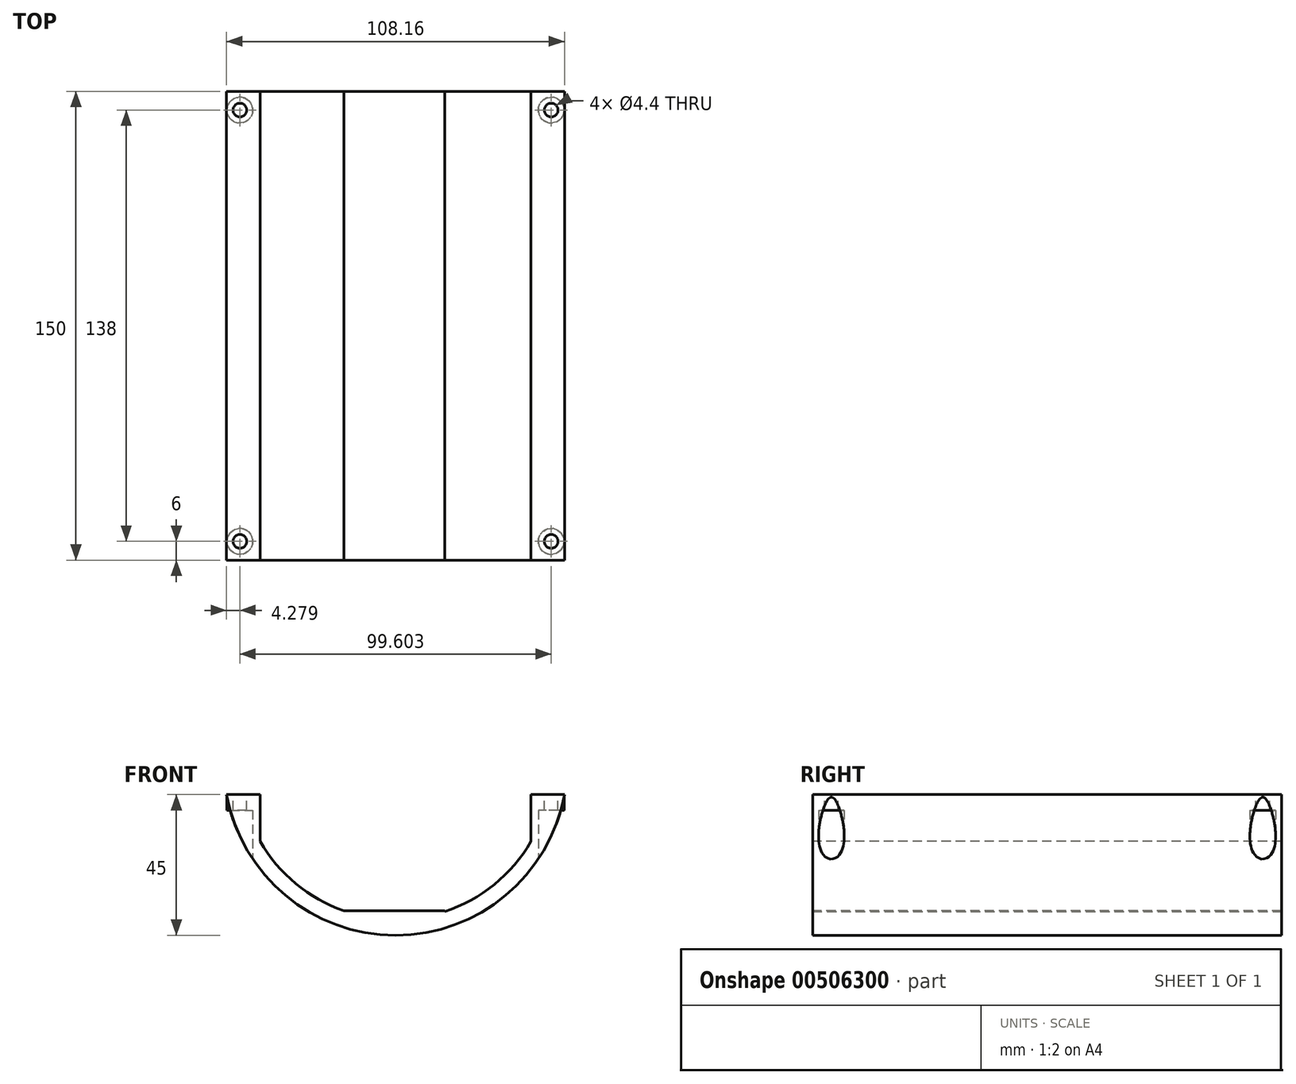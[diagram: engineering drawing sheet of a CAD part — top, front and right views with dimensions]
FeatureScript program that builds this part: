
annotation { "Feature Type Name" : "Feature", "Feature Type Description" : "" }
export const myFeature = defineFeature(function(context is Context, id is Id, definition is map)
    precondition{}
    {
        {
            var Q0;
            Q0=qCreatedBy(makeId("Front.planeOp"),FACE);
            var sketch = newSketch(context, id + "F0", { "sketchPlane" : qUnion([Q0])});
            skCircle(sketch, "E0", {"center": v(0, 0) * mm, "radius": 50 * mm});
            skCircle(sketch, "E1.0", {"center": v(0, 0) * mm, "radius": 55 * mm});
            skSolve(sketch);
        }
        {
            var Q0;
            Q0 = qSketchRegion(id + "F0", true);
            extrude(context, id + "F1", {"entities" : qUnion([Q0]), "depth" : 150 * mm});
        }
        {
            var Q0;
            Q0=makeQuery(id+"F1.opExtrude","CAP_FACE",FACE,{"disambiguationData":[OSD([sQuery(id+"F0.wireOp",EDGE,"E0"),sQuery(id+"F0.wireOp",EDGE,"E1.0")])],"isStart":false});
            var sketch = newSketch(context, id + "F2", { "sketchPlane" : qUnion([Q0])});
            skLineSegment(sketch, "E2.bottom", {"start": v(-54.77, -5) * mm, "end": v(54.77, -5) * mm});
            skLineSegment(sketch, "E2.top", {"start": v(-54.08, -10) * mm, "end": v(54.08, -10) * mm});
            skArc(sketch, "E3.0", {"start": v(-54.77, -5) * mm, "mid": v(-54.49, -7.5) * mm, "end": v(-54.08, -10) * mm});
            skArc(sketch, "E4.trimOffspring", {"start": v(54.08, -10) * mm, "mid": v(54.49, -7.5) * mm, "end": v(54.77, -5) * mm});
            skSolve(sketch);
        }
        {
            var Q0;
            Q0 = qSketchRegion(id + "F2", true);
            extrude(context, id + "F3", {"entities" : qUnion([Q0]), "operationType" : NewBodyOperationType.ADD, "oppositeDirection" : true, "depth" : 150 * mm});
        }
        {
            var Q0;
            Q0=makeQuery(id+"F3.boolean.opBoolean","MERGE",FACE,{"derivedFrom":[makeQuery(id+"F1.opExtrude","CAP_FACE",FACE,{"disambiguationData":[OSD([sQuery(id+"F0.wireOp",EDGE,"E0"),sQuery(id+"F0.wireOp",EDGE,"E1.0")])],"isStart":false}),makeQuery(id+"F3.opExtrude","CAP_FACE",FACE,{"disambiguationData":[OSD([sQuery(id+"F2.wireOp",EDGE,"E2.bottom"),sQuery(id+"F2.wireOp",EDGE,"E2.top"),sQuery(id+"F2.wireOp",EDGE,"E3.0"),sQuery(id+"F2.wireOp",EDGE,"E4.trimOffspring")])],"isStart":true})]});
            var sketch = newSketch(context, id + "F4", { "sketchPlane" : qUnion([Q0])});
            skLineSegment(sketch, "E5", {"start": v(-48.99, 25) * mm, "end": v(48.99, 25) * mm});
            skLineSegment(sketch, "E6", {"start": v(-46.1, 30) * mm, "end": v(46.1, 30) * mm});
            skArc(sketch, "E7.0", {"start": v(48.99, 25) * mm, "mid": v(47.6, 27.54) * mm, "end": v(46.1, 30) * mm});
            skArc(sketch, "E8.trimOffspring", {"start": v(-46.1, 30) * mm, "mid": v(-47.6, 27.54) * mm, "end": v(-48.99, 25) * mm});
            skSolve(sketch);
        }
        {
            var Q0;
            Q0 = qSketchRegion(id + "F4", true);
            extrude(context, id + "F5", {"entities" : qUnion([Q0]), "operationType" : NewBodyOperationType.ADD, "oppositeDirection" : true, "depth" : 150 * mm});
        }
        {
            var Q0;
            Q0=makeQuery(id+"F5.boolean.opBoolean","MERGE",FACE,{"derivedFrom":[makeQuery(id+"F3.boolean.opBoolean","MERGE",FACE,{"derivedFrom":[makeQuery(id+"F1.opExtrude","CAP_FACE",FACE,{"disambiguationData":[OSD([sQuery(id+"F0.wireOp",EDGE,"E0"),sQuery(id+"F0.wireOp",EDGE,"E1.0")])],"isStart":false}),makeQuery(id+"F3.opExtrude","CAP_FACE",FACE,{"disambiguationData":[OSD([sQuery(id+"F2.wireOp",EDGE,"E2.bottom"),sQuery(id+"F2.wireOp",EDGE,"E2.top"),sQuery(id+"F2.wireOp",EDGE,"E3.0"),sQuery(id+"F2.wireOp",EDGE,"E4.trimOffspring")])],"isStart":true})]}),makeQuery(id+"F5.opExtrude","CAP_FACE",FACE,{"disambiguationData":[OSD([sQuery(id+"F4.wireOp",EDGE,"E5"),sQuery(id+"F4.wireOp",EDGE,"E6"),sQuery(id+"F4.wireOp",EDGE,"E7.0"),sQuery(id+"F4.wireOp",EDGE,"E8.trimOffspring")])],"isStart":true})]});
            var sketch = newSketch(context, id + "F6", { "sketchPlane" : qUnion([Q0])});
            skLineSegment(sketch, "E9", {"start": v(-40, 30) * mm, "end": v(108.18, 30) * mm});
            skLineSegment(sketch, "E10", {"start": v(108.18, 30) * mm, "end": v(0, 63.47) * mm});
            skLineSegment(sketch, "E11", {"start": v(0, 63.47) * mm, "end": v(-68.98, 30) * mm});
            skLineSegment(sketch, "E12", {"start": v(-68.98, 30) * mm, "end": v(-40, 30) * mm});
            skSolve(sketch);
        }
        {
            var Q0;
            Q0 = qSketchRegion(id + "F6", true);
            extrude(context, id + "F7", {"entities" : qUnion([Q0]), "operationType" : NewBodyOperationType.REMOVE, "oppositeDirection" : true, "depth" : 233.5 * mm});
        }
        {
            var Q0;
            Q0=makeQuery(id+"F5.boolean.opBoolean","MERGE",FACE,{"derivedFrom":[makeQuery(id+"F3.boolean.opBoolean","MERGE",FACE,{"derivedFrom":[makeQuery(id+"F1.opExtrude","CAP_FACE",FACE,{"disambiguationData":[OSD([sQuery(id+"F0.wireOp",EDGE,"E0"),sQuery(id+"F0.wireOp",EDGE,"E1.0")])],"isStart":false}),makeQuery(id+"F3.opExtrude","CAP_FACE",FACE,{"disambiguationData":[OSD([sQuery(id+"F2.wireOp",EDGE,"E2.bottom"),sQuery(id+"F2.wireOp",EDGE,"E2.top"),sQuery(id+"F2.wireOp",EDGE,"E3.0"),sQuery(id+"F2.wireOp",EDGE,"E4.trimOffspring")])],"isStart":true})]}),makeQuery(id+"F5.opExtrude","CAP_FACE",FACE,{"disambiguationData":[OSD([sQuery(id+"F4.wireOp",EDGE,"E5"),sQuery(id+"F4.wireOp",EDGE,"E6"),sQuery(id+"F4.wireOp",EDGE,"E7.0"),sQuery(id+"F4.wireOp",EDGE,"E8.trimOffspring")])],"isStart":true})]});
            var sketch = newSketch(context, id + "F8", { "sketchPlane" : qUnion([Q0])});
            skLineSegment(sketch, "E13", {"start": v(43.3, 25) * mm, "end": v(43.3, -25) * mm});
            skArc(sketch, "E14.0", {"start": v(43.3, -25) * mm, "mid": v(46.75, -17.73) * mm, "end": v(48.99, -10) * mm});
            skArc(sketch, "E15.0", {"start": v(49.75, -5) * mm, "mid": v(48.88, 10.5) * mm, "end": v(43.3, 25) * mm});
            skPoint(sketch, "E16.orphan", {"position": v(-48.99, -10) * mm});
            skLineSegment(sketch, "E17", {"start": v(49.75, -5) * mm, "end": v(48.99, -10) * mm});
            skLineSegment(sketch, "E18", {"start": v(0, -50) * mm, "end": v(0, -39.73) * mm, "construction": true});
            skPoint(sketch, "E18.endSnap0", {"position": v(0, -50) * mm});
            skLineSegment(sketch, "E19.MirrorCS", {"start": v(-43.3, 25) * mm, "end": v(-43.3, -25) * mm});
            skArc(sketch, "E20.MirrorCS", {"start": v(-43.3, -25) * mm, "mid": v(-46.75, -17.73) * mm, "end": v(-48.99, -10) * mm});
            skLineSegment(sketch, "E21.MirrorCS", {"start": v(-49.75, -5) * mm, "end": v(-48.99, -10) * mm});
            skArc(sketch, "E22.MirrorCS", {"start": v(-49.75, -5) * mm, "mid": v(-48.88, 10.5) * mm, "end": v(-43.3, 25) * mm});
            skSolve(sketch);
        }
        {
            var Q0;
            Q0 = qSketchRegion(id + "F8", true);
            extrude(context, id + "F9", {"entities" : qUnion([Q0]), "operationType" : NewBodyOperationType.ADD, "oppositeDirection" : true, "depth" : 150 * mm});
        }
        {
            var Q0;
            Q0=makeQuery(id+"F9.boolean.opBoolean","MERGE",FACE,{"derivedFrom":[makeQuery(id+"F5.boolean.opBoolean","MERGE",FACE,{"derivedFrom":[makeQuery(id+"F3.boolean.opBoolean","MERGE",FACE,{"derivedFrom":[makeQuery(id+"F1.opExtrude","CAP_FACE",FACE,{"disambiguationData":[OSD([sQuery(id+"F0.wireOp",EDGE,"E0"),sQuery(id+"F0.wireOp",EDGE,"E1.0")])],"isStart":false}),makeQuery(id+"F3.opExtrude","CAP_FACE",FACE,{"disambiguationData":[OSD([sQuery(id+"F2.wireOp",EDGE,"E2.bottom"),sQuery(id+"F2.wireOp",EDGE,"E2.top"),sQuery(id+"F2.wireOp",EDGE,"E3.0"),sQuery(id+"F2.wireOp",EDGE,"E4.trimOffspring")])],"isStart":true})]}),makeQuery(id+"F5.opExtrude","CAP_FACE",FACE,{"disambiguationData":[OSD([sQuery(id+"F4.wireOp",EDGE,"E5"),sQuery(id+"F4.wireOp",EDGE,"E6"),sQuery(id+"F4.wireOp",EDGE,"E7.0"),sQuery(id+"F4.wireOp",EDGE,"E8.trimOffspring")])],"isStart":true})]}),makeQuery(id+"F9.opExtrude","CAP_FACE",FACE,{"disambiguationData":[OSD([sQuery(id+"F8.wireOp",EDGE,"E13"),sQuery(id+"F8.wireOp",EDGE,"E14.0"),sQuery(id+"F8.wireOp",EDGE,"E15.0"),sQuery(id+"F8.wireOp",EDGE,"E17")])],"isStart":true}),makeQuery(id+"F9.opExtrude","CAP_FACE",FACE,{"disambiguationData":[OSD([sQuery(id+"F8.wireOp",EDGE,"E19.MirrorCS"),sQuery(id+"F8.wireOp",EDGE,"E20.MirrorCS"),sQuery(id+"F8.wireOp",EDGE,"E21.MirrorCS"),sQuery(id+"F8.wireOp",EDGE,"E22.MirrorCS")])],"isStart":true})]});
            var sketch = newSketch(context, id + "F10", { "sketchPlane" : qUnion([Q0])});
            skLineSegment(sketch, "E23.bottom", {"start": v(15.68, -50.82) * mm, "end": v(-16.53, -50.82) * mm});
            skLineSegment(sketch, "E23.top", {"start": v(15.68, -47.19) * mm, "end": v(-16.53, -47.19) * mm});
            skLineSegment(sketch, "E23.left", {"start": v(15.68, -50.82) * mm, "end": v(15.68, -47.19) * mm});
            skLineSegment(sketch, "E23.right", {"start": v(-16.53, -50.82) * mm, "end": v(-16.53, -47.19) * mm});
            skSolve(sketch);
        }
        {
            var Q0;
            Q0 = qSketchRegion(id + "F10", true);
            extrude(context, id + "F11", {"entities" : qUnion([Q0]), "operationType" : NewBodyOperationType.ADD, "oppositeDirection" : true, "depth" : 150 * mm});
        }
        {
            var Q0;
            Q0=makeQuery(id+"F3.opExtrude","SWEPT_FACE",FACE,{"disambiguationData":[OSD([sQuery(id+"F2.wireOp",EDGE,"E2.top")])]});
            cPlane(context, id + "F12", {"entities" : qUnion([Q0]), "cplaneType" : CPlaneType.OFFSET, "offset" : 10 * mm, "width" : 150 * mm, "height" : 150 * mm});
        }
        {
            var Q0;
            Q0=qCreatedBy(id+"F12.planeOp",FACE);
            var sketch = newSketch(context, id + "F13", { "sketchPlane" : qUnion([Q0])});
            skLineSegment(sketch, "E24", {"start": v(49.8, 144) * mm, "end": v(49.8, 4.23) * mm, "construction": true});
            skPoint(sketch, "E25", {"position": v(49.8, 6) * mm});
            skPoint(sketch, "E26", {"position": v(49.8, -57) * mm});
            skPoint(sketch, "E27", {"position": v(49.8, 144) * mm});
            skLineSegment(sketch, "E28", {"start": v(0, 0) * mm, "end": v(0, -24.3) * mm, "construction": true});
            skPoint(sketch, "E29.MirrorP", {"position": v(-49.8, 6) * mm});
            skPoint(sketch, "E30.MirrorP", {"position": v(-49.8, -57) * mm});
            skPoint(sketch, "E31.MirrorP", {"position": v(-49.8, 144) * mm});
            skSolve(sketch);
        }
        {
            var Q0;
            Q0=sQuery(id+"F13.wireOp",VERTEX,"E25");
            var Q1;
            Q1=sQuery(id+"F13.wireOp",VERTEX,"E29.MirrorP");
            var Q2;
            Q2=sQuery(id+"F13.wireOp",VERTEX,"E27");
            var Q3;
            Q3=sQuery(id+"F13.wireOp",VERTEX,"E31.MirrorP");
            var Q4;
            Q4=makeQuery(id+"F1.opExtrude","SWEPT_BODY",BODY,{"disambiguationData":[OSD([sQuery(id+"F0.wireOp",EDGE,"E0"),sQuery(id+"F0.wireOp",EDGE,"E1.0")])]});
            hole(context, id + "F14", {"style" : HoleStyle.C_BORE, "endStyle" : HoleEndStyle.BLIND, "holeDiameter" : 4.4 * mm, "cBoreDiameter" : 8.25 * mm, "cBoreDepth" : 10 * mm, "holeDepth" : 50 * mm, "isTappedThrough" : true, "tappedDepth" : 12 * mm, "tapClearance" : 3, "startFromSketch" : true, "locations" : qUnion([Q0, Q1, Q2, Q3]), "scope" : qUnion([Q4])});
        }
        {
            var Q0;
            Q0=qCreatedBy(id+"F12.planeOp",FACE);
            var sketch = newSketch(context, id + "F15", { "sketchPlane" : qUnion([Q0])});
            skArc(sketch, "E32.0", {"start": v(51.23, 147.87) * mm, "mid": v(45.68, 144) * mm, "end": v(51.23, 140.13) * mm});
            skArc(sketch, "E33.0", {"start": v(51.23, 140.13) * mm, "mid": v(53.93, 144) * mm, "end": v(51.23, 147.87) * mm});
            skArc(sketch, "E34.0", {"start": v(51.23, 2.13) * mm, "mid": v(53.93, 6) * mm, "end": v(51.23, 9.87) * mm});
            skArc(sketch, "E35.0", {"start": v(51.23, 9.87) * mm, "mid": v(45.68, 6) * mm, "end": v(51.23, 2.13) * mm});
            skArc(sketch, "E36.0", {"start": v(-51.23, 140.13) * mm, "mid": v(-45.68, 144) * mm, "end": v(-51.23, 147.87) * mm});
            skArc(sketch, "E37.0", {"start": v(-51.23, 147.87) * mm, "mid": v(-53.93, 144) * mm, "end": v(-51.23, 140.13) * mm});
            skArc(sketch, "E38.0", {"start": v(-51.23, 9.87) * mm, "mid": v(-53.93, 6) * mm, "end": v(-51.23, 2.13) * mm});
            skArc(sketch, "E39.0", {"start": v(-51.23, 2.13) * mm, "mid": v(-45.68, 6) * mm, "end": v(-51.23, 9.87) * mm});
            skSolve(sketch);
        }
        {
            var Q0;
            Q0 = qSketchRegion(id + "F15", true);
            extrude(context, id + "F16", {"entities" : qUnion([Q0]), "operationType" : NewBodyOperationType.REMOVE, "oppositeDirection" : true, "depth" : 90.2 * mm, "hasSecondDirection" : true, "secondDirectionOppositeDirection" : true, "secondDirectionDepth" : 15 * mm});
        }
        {
            var Q0;
            Q0 = qSketchRegion(id + "F15", true);
            extrude(context, id + "F17", {"entities" : qUnion([Q0]), "operationType" : NewBodyOperationType.REMOVE, "depth" : 25 * mm});
        }
        {
            var Q0;
            Q0=makeQuery(id+"F11.boolean.opBoolean","MERGE",FACE,{"derivedFrom":[makeQuery(id+"F9.boolean.opBoolean","MERGE",FACE,{"derivedFrom":[makeQuery(id+"F5.boolean.opBoolean","MERGE",FACE,{"derivedFrom":[makeQuery(id+"F3.boolean.opBoolean","MERGE",FACE,{"derivedFrom":[makeQuery(id+"F1.opExtrude","CAP_FACE",FACE,{"disambiguationData":[OSD([sQuery(id+"F0.wireOp",EDGE,"E0"),sQuery(id+"F0.wireOp",EDGE,"E1.0")])],"isStart":true}),makeQuery(id+"F3.opExtrude","CAP_FACE",FACE,{"disambiguationData":[OSD([sQuery(id+"F2.wireOp",EDGE,"E2.bottom"),sQuery(id+"F2.wireOp",EDGE,"E2.top"),sQuery(id+"F2.wireOp",EDGE,"E3.0"),sQuery(id+"F2.wireOp",EDGE,"E4.trimOffspring")])],"isStart":false})]}),makeQuery(id+"F5.opExtrude","CAP_FACE",FACE,{"disambiguationData":[OSD([sQuery(id+"F4.wireOp",EDGE,"E5"),sQuery(id+"F4.wireOp",EDGE,"E6"),sQuery(id+"F4.wireOp",EDGE,"E7.0"),sQuery(id+"F4.wireOp",EDGE,"E8.trimOffspring")])],"isStart":false})]}),makeQuery(id+"F9.opExtrude","CAP_FACE",FACE,{"disambiguationData":[OSD([sQuery(id+"F8.wireOp",EDGE,"E13"),sQuery(id+"F8.wireOp",EDGE,"E14.0"),sQuery(id+"F8.wireOp",EDGE,"E15.0"),sQuery(id+"F8.wireOp",EDGE,"E17")])],"isStart":false}),makeQuery(id+"F9.opExtrude","CAP_FACE",FACE,{"disambiguationData":[OSD([sQuery(id+"F8.wireOp",EDGE,"E19.MirrorCS"),sQuery(id+"F8.wireOp",EDGE,"E20.MirrorCS"),sQuery(id+"F8.wireOp",EDGE,"E21.MirrorCS"),sQuery(id+"F8.wireOp",EDGE,"E22.MirrorCS")])],"isStart":false})]}),makeQuery(id+"F11.opExtrude","CAP_FACE",FACE,{"disambiguationData":[OSD([sQuery(id+"F10.wireOp",EDGE,"E23.bottom"),sQuery(id+"F10.wireOp",EDGE,"E23.top"),sQuery(id+"F10.wireOp",EDGE,"E23.left"),sQuery(id+"F10.wireOp",EDGE,"E23.right")])],"isStart":false})]});
            var sketch = newSketch(context, id + "F18", { "sketchPlane" : qUnion([Q0])});
            skLineSegment(sketch, "E40.bottom", {"start": v(43.3, -10) * mm, "end": v(-79.43, -10) * mm});
            skLineSegment(sketch, "E40.top", {"start": v(43.3, 37.57) * mm, "end": v(-79.43, 37.57) * mm});
            skLineSegment(sketch, "E40.right", {"start": v(-79.43, -10) * mm, "end": v(-79.43, 37.57) * mm});
            skLineSegment(sketch, "E41.bottom", {"start": v(43.3, -10) * mm, "end": v(89.9, -10) * mm});
            skLineSegment(sketch, "E41.top", {"start": v(43.3, 37.57) * mm, "end": v(89.9, 37.57) * mm});
            skLineSegment(sketch, "E41.right", {"start": v(89.9, -10) * mm, "end": v(89.9, 37.57) * mm});
            skSolve(sketch);
        }
        {
            var Q0;
            Q0 = qSketchRegion(id + "F18", true);
            extrude(context, id + "F19", {"entities" : qUnion([Q0]), "operationType" : NewBodyOperationType.REMOVE, "oppositeDirection" : true, "depth" : 190.1 * mm});
        }
        {
            var Q0;
            {var subQ0=sQuery(id+"F8.wireOp",EDGE,"E19.MirrorCS");Q0=makeQuery(id+"F19.boolean.opBoolean","COPY",FACE,{"disambiguationData":[TD([makeQuery(id+"F9.opExtrude","SWEPT_FACE",FACE,{"disambiguationData":[OSD([subQ0])]})])],"derivedFrom":makeQuery(id+"F19.opExtrude","SWEPT_FACE",FACE,{"disambiguationData":[OSD([sQuery(id+"F18.wireOp",EDGE,"E40.bottom"),sQuery(id+"F18.wireOp",EDGE,"E41.bottom")])]})});}
            var sketch = newSketch(context, id + "F20", { "sketchPlane" : qUnion([Q0])});
            skCircle(sketch, "E42.0", {"center": v(-49.8, -144) * mm, "radius": 4.12 * mm});
            skCircle(sketch, "E43.0", {"center": v(-49.8, -6) * mm, "radius": 4.12 * mm});
            skCircle(sketch, "E44.0", {"center": v(49.8, -144) * mm, "radius": 4.12 * mm});
            skCircle(sketch, "E45.0", {"center": v(49.8, -6) * mm, "radius": 4.12 * mm});
            skCircle(sketch, "E46", {"center": v(-49.8, -144) * mm, "radius": 2.2 * mm});
            skCircle(sketch, "E47", {"center": v(-49.8, -6) * mm, "radius": 2.2 * mm});
            skCircle(sketch, "E48", {"center": v(49.8, -144) * mm, "radius": 2.2 * mm});
            skCircle(sketch, "E49", {"center": v(49.8, -6) * mm, "radius": 2.2 * mm});
            skSolve(sketch);
        }
        {
            var Q0;
            Q0 = qSketchRegion(id + "F20", true);
            extrude(context, id + "F21", {"entities" : qUnion([Q0]), "operationType" : NewBodyOperationType.ADD, "oppositeDirection" : true, "depth" : 5 * mm, "offsetDistance" : 25 * mm});
        }
    });
